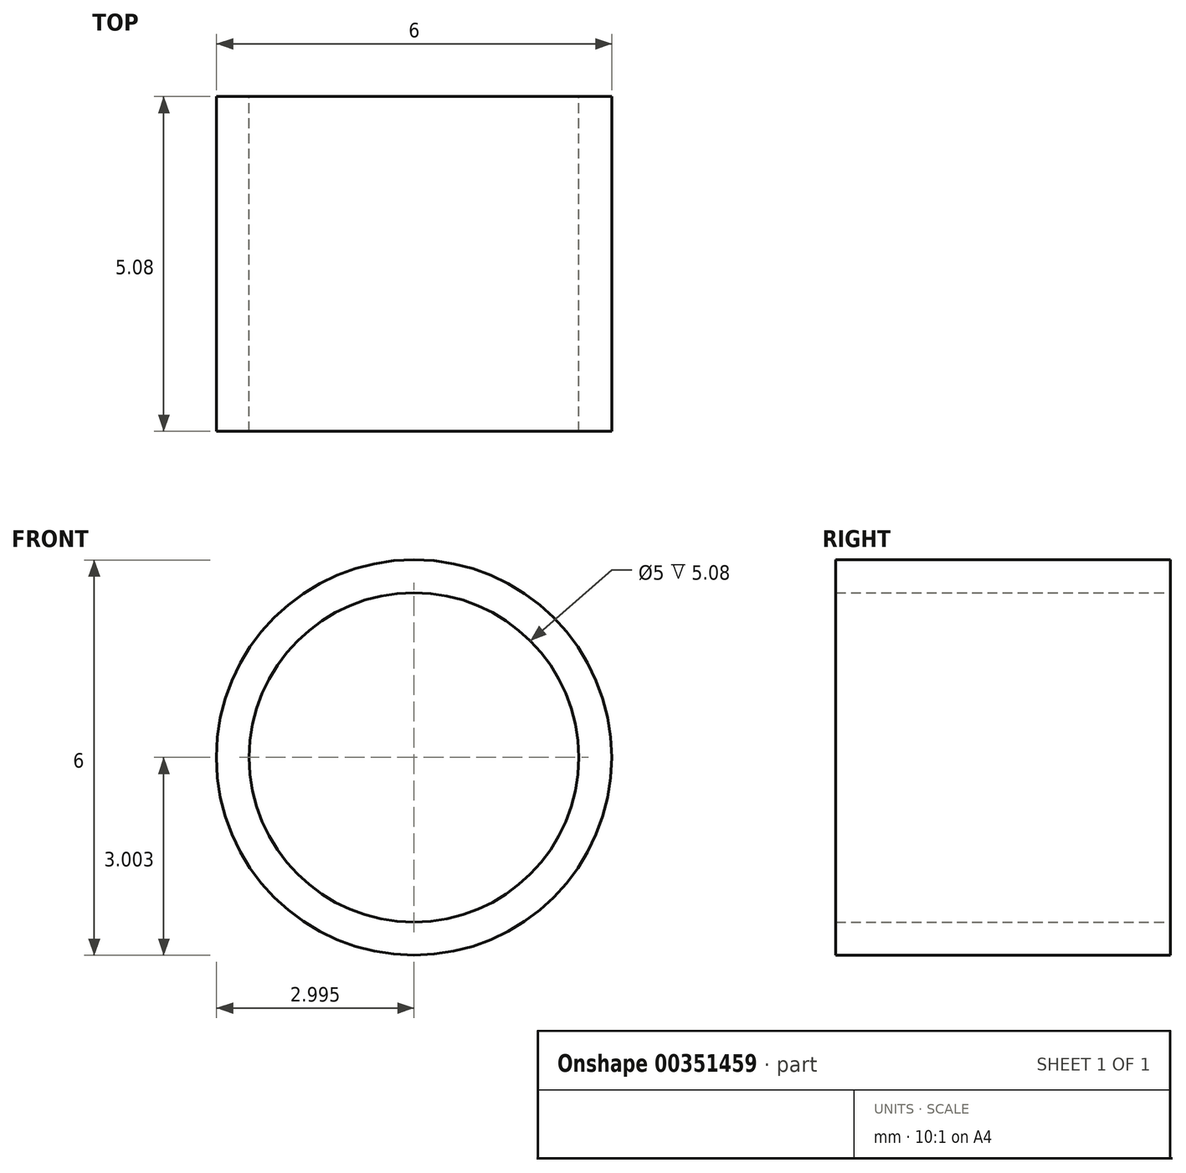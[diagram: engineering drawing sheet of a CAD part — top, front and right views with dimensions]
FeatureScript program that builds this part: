
annotation { "Feature Type Name" : "Feature", "Feature Type Description" : "" }
export const myFeature = defineFeature(function(context is Context, id is Id, definition is map)
    precondition{}
    {
        {
            var Q0;
            Q0=qCreatedBy(makeId("Front.planeOp"),FACE);
            var sketch = newSketch(context, id + "F0", { "sketchPlane" : qUnion([Q0])});
            skCircle(sketch, "E0", {"center": v(-38.47, 19.38) * mm, "radius": 3 * mm});
            skCircle(sketch, "E1", {"center": v(-38.47, 19.38) * mm, "radius": 2.5 * mm});
            skSolve(sketch);
        }
        {
            var Q0;
            Q0=makeQuery(id+"F0.imprint","IMPRINT",FACE,{"disambiguationData":[TD([[makeQuery(id+"F0.imprint","IMPRINT",EDGE,{"derivedFrom":sQuery(id+"F0.wireOp",EDGE,"E0")}),1.0]])]});
            extrude(context, id + "F1", {"entities" : qUnion([Q0]), "depth" : 5.08 * mm});
        }
    });
